# Revit family: VKDV_К2_Eng
name_source: partatom
category: Оборудование
units: mm (PartAtom-declared; Revit-internal decimal feet)

## family parameters
Всегда вертикально = Да
Классификация = Нет
На основе рабочей плоскости = Нет
Общий = Нет
При загрузке вырезать с полостями = Нет
Размер круглого соединителя = Использовать диаметр
Тип детали = Нормальный
Точка принадлежности помещению = Нет

## types (36) — shared parameters
00_20_Manufacturer = Vents
00_20_Name = Roof-mounted smoke extraction fan
Casing Material = Metal, painted, blue, matte RAL 5007
Frequency = 50 Гц
Grid Material = Mesh, steel, painted, RAL5007
Load Classification = HVAC
Maintenance zone material = <По категории>
Number of Fase = 3
URL = https://ventilation-system.com
Voltage = 400 В
Изготовитель = Vents
zero-valued in all types: Отметка по умолчанию

## per-type parameters (varying)
| type | A | B | C | H | Height | Kh | Kl | Length | Maximum Air Flow | Power | R | Weight | Width | h | h1 | h2 | Ш | Ш1 | Ш2 | Ш3 | ш | ш1 |
| VKDV-K2-710-4D/11-K | 1180 мм | 980 мм | 1267 мм | 1264 мм | 1264 мм | 50 мм | 100 мм | 1267 мм | 28080.0 м³/ч | 11000 Вт | 441 мм | 342.00 кг | 1180 мм | 421 мм | 296 мм | 393 мм | 1180 мм | 590 мм | 229 мм | 246 мм | 1100 мм | 550 мм |
| VKDV-K2-800-6D/4-K | 1180 мм | 980 мм | 1311 мм | 1237 мм | 1237 мм | 50 мм | 100 мм | 1311 мм | 25020.0 м³/ч | 4000 Вт | 441 мм | 311.00 кг | 1180 мм | 412 мм | 296 мм | 393 мм | 1180 мм | 590 мм | 229 мм | 246 мм | 1100 мм | 550 мм |
| VKDV-K2-1120-8D/15-K | 1640 мм | 1340 мм | 1876 мм | 1866 мм | 1866 мм | 75 мм | 150 мм | 1876 мм | 63000.0 м³/ч | 15000 Вт | 603 мм | 911.00 кг | 1640 мм | 622 мм | 392 мм | 547 мм | 1640 мм | 820 мм | 318 мм | 342 мм | 1560 мм | 780 мм |
| VKDV-K2-630-8D/0,75-K | 1010 мм | 750 мм | 1121 мм | 1060 мм | 1060 мм | 50 мм | 100 мм | 1121 мм | 9000.0 м³/ч | 750 Вт | 338 мм | 200.00 кг | 1010 мм | 353 мм | 260 мм | 337 мм | 1010 мм | 505 мм | 196 мм | 210 мм | 930 мм | 465 мм |
| VKDV-K2-630-4D/5,5-K | 1010 мм | 750 мм | 1121 мм | 1060 мм | 1060 мм | 50 мм | 100 мм | 1121 мм | 18720.0 м³/ч | 5500 Вт | 338 мм | 225.00 кг | 1010 мм | 353 мм | 260 мм | 337 мм | 1010 мм | 505 мм | 196 мм | 210 мм | 930 мм | 465 мм |
| VKDV-K2-710-8D/1,1-K | 1180 мм | 980 мм | 1257 мм | 1105 мм | 1105 мм | 50 мм | 100 мм | 1257 мм | 12960.0 м³/ч | 1100 Вт | 441 мм | 231.00 кг | 1180 мм | 368 мм | 296 мм | 393 мм | 1180 мм | 590 мм | 229 мм | 246 мм | 1100 мм | 550 мм |
| VKDV-K2-710-6D/2,2-K | 1180 мм | 980 мм | 1257 мм | 1105 мм | 1105 мм | 50 мм | 100 мм | 1257 мм | 17280.0 м³/ч | 2200 Вт | 441 мм | 238.00 кг | 1180 мм | 368 мм | 296 мм | 393 мм | 1180 мм | 590 мм | 229 мм | 246 мм | 1100 мм | 550 мм |
| VKDV-K2-800-8D/2,2-K | 1180 мм | 980 мм | 1311 мм | 1237 мм | 1237 мм | 50 мм | 100 мм | 1311 мм | 19080.0 м³/ч | 2200 Вт | 441 мм | 308.00 кг | 1180 мм | 412 мм | 296 мм | 393 мм | 1180 мм | 590 мм | 229 мм | 246 мм | 1100 мм | 550 мм |
| VKDV-K2-800-4D/15-K | 1180 мм | 980 мм | 1311 мм | 1387 мм | 1387 мм | 50 мм | 100 мм | 1311 мм | 38880.0 м³/ч | 15000 Вт | 441 мм | 385.00 кг | 1180 мм | 462 мм | 296 мм | 393 мм | 1180 мм | 590 мм | 229 мм | 246 мм | 1100 мм | 550 мм |
| VKDV-K2-900-10D/2,2-K | 1340 мм | 1050 мм | 1494 мм | 1297 мм | 1297 мм | 50 мм | 100 мм | 1494 мм | 22500.0 м³/ч | 2200 Вт | 473 мм | 374.00 кг | 1340 мм | 432 мм | 329 мм | 447 мм | 1340 мм | 670 мм | 260 мм | 279 мм | 1260 мм | 630 мм |
| VKDV-K2-900-8D/4-K | 1340 мм | 1050 мм | 1494 мм | 1448 мм | 1448 мм | 50 мм | 100 мм | 1494 мм | 27000.0 м³/ч | 4000 Вт | 473 мм | 435.00 кг | 1340 мм | 483 мм | 329 мм | 447 мм | 1340 мм | 670 мм | 260 мм | 279 мм | 1260 мм | 630 мм |
| VKDV-K2-900-6D/7,5-K | 1340 мм | 1050 мм | 1494 мм | 1448 мм | 1448 мм | 50 мм | 100 мм | 1494 мм | 37800.0 м³/ч | 7500 Вт | 473 мм | 434.00 кг | 1340 мм | 483 мм | 329 мм | 447 мм | 1340 мм | 670 мм | 260 мм | 279 мм | 1260 мм | 630 мм |
| VKDV-K2-900-4D/30-K | 1340 мм | 1050 мм | 1524 мм | 1600 мм | 1600 мм | 50 мм | 100 мм | 1524 мм | 55800.0 м³/ч | 30000 Вт | 473 мм | 597.00 кг | 1340 мм | 533 мм | 329 мм | 447 мм | 1340 мм | 670 мм | 260 мм | 279 мм | 1260 мм | 630 мм |
| VKDV-K2-1000-10D/3-K | 1550 мм | 1340 мм | 1686 мм | 1595 мм | 1595 мм | 75 мм | 150 мм | 1686 мм | 32400.0 м³/ч | 3000 Вт | 603 мм | 573.00 кг | 1550 мм | 532 мм | 373 мм | 517 мм | 1550 мм | 775 мм | 301 мм | 323 мм | 1470 мм | 735 мм |
| VKDV-K2-1000-8D/7,5-K | 1550 мм | 1340 мм | 1686 мм | 1595 мм | 1595 мм | 75 мм | 150 мм | 1686 мм | 38880.0 м³/ч | 7500 Вт | 603 мм | 557.00 кг | 1550 мм | 532 мм | 373 мм | 517 мм | 1550 мм | 775 мм | 301 мм | 323 мм | 1470 мм | 735 мм |
| VKDV-K2-1000-6D/15-K | 1550 мм | 1340 мм | 1686 мм | 1680 мм | 1680 мм | 75 мм | 150 мм | 1686 мм | 54000.0 м³/ч | 15000 Вт | 603 мм | 608.00 кг | 1550 мм | 560 мм | 373 мм | 517 мм | 1550 мм | 775 мм | 301 мм | 323 мм | 1470 мм | 735 мм |
| VKDV-K2-1120-10D/7,5-K | 1640 мм | 1340 мм | 1876 мм | 1829 мм | 1829 мм | 75 мм | 150 мм | 1876 мм | 49680.0 м³/ч | 7500 Вт | 603 мм | 834.00 кг | 1640 мм | 610 мм | 392 мм | 547 мм | 1640 мм | 820 мм | 318 мм | 342 мм | 1560 мм | 780 мм |
| VKDV-K2-1120-8D/11-K | 1640 мм | 1340 мм | 1876 мм | 1753 мм | 1753 мм | 75 мм | 150 мм | 1876 мм | 54000.0 м³/ч | 11000 Вт | 603 мм | 834.00 кг | 1640 мм | 584 мм | 392 мм | 547 мм | 1640 мм | 820 мм | 318 мм | 342 мм | 1560 мм | 780 мм |
| VKDV-K2-630-6D/1,5-K | 1010 мм | 750 мм | 1121 мм | 1060 мм | 1060 мм | 50 мм | 100 мм | 1121 мм | 12600.0 м³/ч | 1500 Вт | 338 мм | 202.00 кг | 1010 мм | 353 мм | 260 мм | 337 мм | 1010 мм | 505 мм | 196 мм | 210 мм | 930 мм | 465 мм |
| VKDV-K2-1120-6D/22-K | 1640 мм | 1340 мм | 1876 мм | 1789 мм | 1789 мм | 75 мм | 150 мм | 1876 мм | 74880.0 м³/ч | 22000 Вт | 603 мм | 856.00 кг | 1640 мм | 596 мм | 392 мм | 547 мм | 1640 мм | 820 мм | 318 мм | 342 мм | 1560 мм | 780 мм |
| VKDV-K2-1120-6D/30-K | 1640 мм | 1340 мм | 1876 мм | 1956 мм | 1956 мм | 75 мм | 150 мм | 1876 мм | 84600.0 м³/ч | 30000 Вт | 603 мм | 962.00 кг | 1640 мм | 652 мм | 392 мм | 547 мм | 1640 мм | 820 мм | 318 мм | 342 мм | 1560 мм | 780 мм |
| VKDV-K2-560-4D/3-K | 1000 мм | 750 мм | 1094 мм | 991 мм | 991 мм | 50 мм | 100 мм | 1094 мм | 13500.0 м³/ч | 3000 Вт | 338 мм | 163.00 кг | 1000 мм | 330 мм | 258 мм | 333 мм | 1000 мм | 500 мм | 194 мм | 208 мм | 920 мм | 460 мм |
| VKDV-K2-560-6D/0,75-K | 1000 мм | 750 мм | 1082 мм | 921 мм | 921 мм | 50 мм | 100 мм | 1082 мм | 8640.0 м³/ч | 750 Вт | 338 мм | 151.00 кг | 1000 мм | 307 мм | 258 мм | 333 мм | 1000 мм | 500 мм | 194 мм | 208 мм | 920 мм | 460 мм |
| VKDV-K2-560-8D/0,37-K | 1000 мм | 750 мм | 1082 мм | 921 мм | 921 мм | 50 мм | 100 мм | 1082 мм | 6480.0 м³/ч | 370 Вт | 338 мм | 148.00 кг | 1000 мм | 307 мм | 258 мм | 333 мм | 1000 мм | 500 мм | 194 мм | 208 мм | 920 мм | 460 мм |
| VKDV-K2-500-4D/1,5-K | 830 мм | 640 мм | 950 мм | 888 мм | 888 мм | 50 мм | 100 мм | 950 мм | 9720.0 м³/ч | 1500 Вт | 288 мм | 128.00 кг | 830 мм | 296 мм | 223 мм | 277 мм | 830 мм | 415 мм | 161 мм | 173 мм | 750 мм | 375 мм |
| VKDV-K2-500-6D/0,55-K | 830 мм | 640 мм | 950 мм | 888 мм | 888 мм | 50 мм | 100 мм | 950 мм | 3960.0 м³/ч | 550 Вт | 288 мм | 122.00 кг | 830 мм | 296 мм | 223 мм | 277 мм | 830 мм | 415 мм | 161 мм | 173 мм | 750 мм | 375 мм |
| VKDV-K2-500-8D/0,25-K | 830 мм | 640 мм | 950 мм | 888 мм | 888 мм | 50 мм | 100 мм | 950 мм | 1512.0 м³/ч | 250 Вт | 288 мм | 121.00 кг | 830 мм | 296 мм | 223 мм | 277 мм | 830 мм | 415 мм | 161 мм | 173 мм | 750 мм | 375 мм |
| VKDV-K2-450-2D/7,5-K | 810 мм | 580 мм | 933 мм | 929 мм | 929 мм | 50 мм | 100 мм | 933 мм | 13680.0 м³/ч | 7500 Вт | 261 мм | 137.00 кг | 810 мм | 310 мм | 219 мм | 270 мм | 810 мм | 405 мм | 157 мм | 169 мм | 730 мм | 365 мм |
| VKDV-K2-450-4D/1,1-K | 760 мм | 580 мм | 864 мм | 794 мм | 794 мм | 50 мм | 100 мм | 864 мм | 6750.0 м³/ч | 1100 Вт | 261 мм | 96.00 кг | 760 мм | 265 мм | 208 мм | 253 мм | 760 мм | 380 мм | 148 мм | 158 мм | 680 мм | 340 мм |
| VKDV-K2-450-6D/0,25-K | 760 мм | 580 мм | 864 мм | 794 мм | 794 мм | 50 мм | 100 мм | 864 мм | 3960.0 м³/ч | 250 Вт | 261 мм | 92.00 кг | 760 мм | 265 мм | 208 мм | 253 мм | 760 мм | 380 мм | 148 мм | 158 мм | 680 мм | 340 мм |
| VKDV-K2-400-2D/4-K | 760 мм | 580 мм | 880 мм | 897 мм | 897 мм | 50 мм | 100 мм | 880 мм | 9360.0 м³/ч | 4000 Вт | 261 мм | 112.00 кг | 760 мм | 299 мм | 208 мм | 253 мм | 760 мм | 380 мм | 148 мм | 158 мм | 680 мм | 340 мм |
| VKDV-K2-400-4D/0,55-K | 760 мм | 580 мм | 866 мм | 772 мм | 772 мм | 50 мм | 100 мм | 866 мм | 4500.0 м³/ч | 550 Вт | 261 мм | 83.00 кг | 760 мм | 257 мм | 208 мм | 253 мм | 760 мм | 380 мм | 148 мм | 158 мм | 680 мм | 340 мм |
| VKDV-K2-400-6D/0,25-K | 760 мм | 580 мм | 866 мм | 772 мм | 772 мм | 50 мм | 100 мм | 866 мм | 2880.0 м³/ч | 250 Вт | 261 мм | 82.00 кг | 760 мм | 257 мм | 208 мм | 253 мм | 760 мм | 380 мм | 148 мм | 158 мм | 680 мм | 340 мм |
| VKDV-K2-355-2D/2,2-K | 680 мм | 480 мм | 820 мм | 801 мм | 801 мм | 50 мм | 100 мм | 820 мм | 6750.0 м³/ч | 2200 Вт | 216 мм | 89.00 кг | 680 мм | 267 мм | 192 мм | 227 мм | 680 мм | 340 мм | 132 мм | 142 мм | 600 мм | 300 мм |
| VKDV-K2-355-4D/0,25-K | 680 мм | 480 мм | 820 мм | 744 мм | 744 мм | 50 мм | 100 мм | 820 мм | 3168.0 м³/ч | 250 Вт | 216 мм | 73.00 кг | 680 мм | 248 мм | 192 мм | 227 мм | 680 мм | 340 мм | 132 мм | 142 мм | 600 мм | 300 мм |
| VKDV-K2-315-2D/1,1-K | 680 мм | 480 мм | 820 мм | 779 мм | 779 мм | 50 мм | 100 мм | 820 мм | 4680.0 м³/ч | 1100 Вт | 216 мм | 80.00 кг | 680 мм | 260 мм | 192 мм | 227 мм | 680 мм | 340 мм | 132 мм | 142 мм | 600 мм | 300 мм |

note: column(s) folded — value = type name in every type: 00_20_Type
